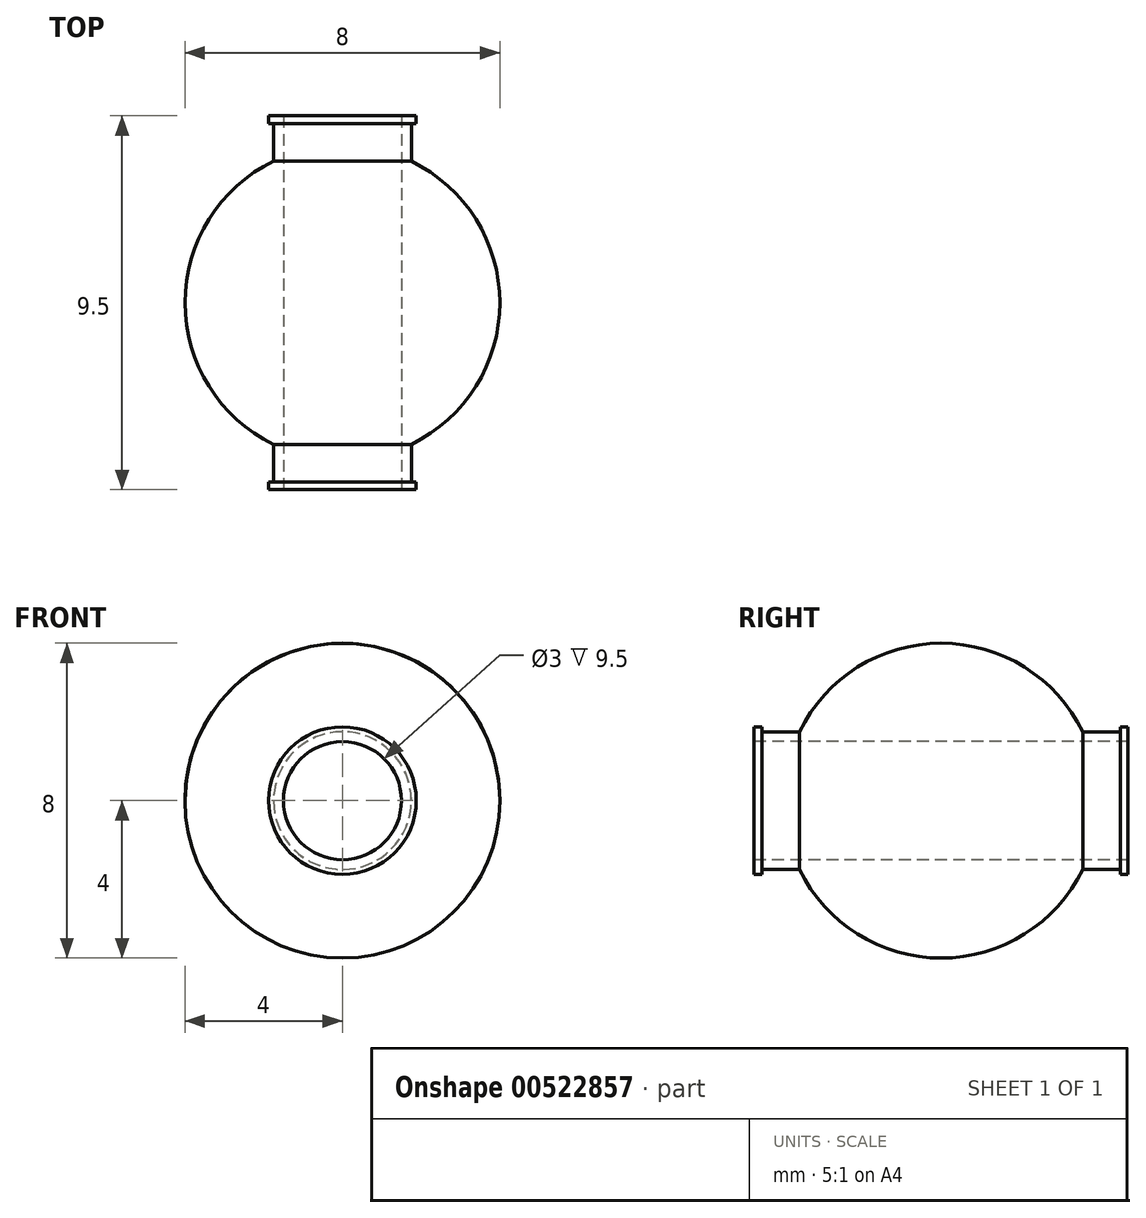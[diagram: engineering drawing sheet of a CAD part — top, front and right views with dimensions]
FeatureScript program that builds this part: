
annotation { "Feature Type Name" : "Feature", "Feature Type Description" : "" }
export const myFeature = defineFeature(function(context is Context, id is Id, definition is map)
    precondition{}
    {
        {
            var Q0;
            Q0=qCreatedBy(makeId("Front.planeOp"),FACE);
            var sketch = newSketch(context, id + "F0", { "sketchPlane" : qUnion([Q0])});
            skCircle(sketch, "E0", {"center": v(0, 0) * mm, "radius": 4 * mm});
            skLineSegment(sketch, "E1", {"start": v(-18.18, 0) * mm, "end": v(24.7, 0) * mm});
            skSolve(sketch);
        }
        {
            var Q0;
            {var subQ0=sQuery(id+"F0.wireOp",EDGE,"E1");var subQ1=sQuery(id+"F0.wireOp",EDGE,"E0");var subQ2=makeQuery(id+"F0.imprint","INTERSECT",VERTEX,{"disambiguationData":[OD(0.0)],"derivedFrom":[subQ1,subQ0]});Q0=makeQuery(id+"F0.imprint","IMPRINT",FACE,{"disambiguationData":[TD([[makeQuery(id+"F0.imprint","IMPRINT",EDGE,{"disambiguationData":[TD([[subQ2,1.0]])],"derivedFrom":subQ1}),1.0]])]});}
            var Q1;
            Q1=sQuery(id+"F0.wireOp",EDGE,"E1");
            revolve(context, id + "F1", {"surfaceOperationType" : NewSurfaceOperationType.NEW, "entities" : qUnion([Q0]), "axis" : qUnion([Q1]), "revolveType" : RevolveType.FULL});
        }
        {
            var Q0;
            Q0=qCreatedBy(makeId("Front.planeOp"),FACE);
            var sketch = newSketch(context, id + "F2", { "sketchPlane" : qUnion([Q0])});
            skCircle(sketch, "E2", {"center": v(0, 0) * mm, "radius": 1.5 * mm});
            skCircle(sketch, "E3", {"center": v(0, 0) * mm, "radius": 1.75 * mm});
            skSolve(sketch);
        }
        {
            var Q0;
            Q0=makeQuery(id+"F2.imprint","IMPRINT",FACE,{"disambiguationData":[TD([[makeQuery(id+"F2.imprint","IMPRINT",EDGE,{"derivedFrom":sQuery(id+"F2.wireOp",EDGE,"E2")}),1.0]])]});
            extrude(context, id + "F3", {"entities" : qUnion([Q0]), "operationType" : NewBodyOperationType.REMOVE, "endBound" : BoundingType.SYMMETRIC, "oppositeDirection" : true, "depth" : 25 * mm, "offsetDistance" : 25 * mm});
        }
        {
            var Q0;
            Q0=makeQuery(id+"F2.imprint","IMPRINT",FACE,{"disambiguationData":[TD([[makeQuery(id+"F2.imprint","IMPRINT",EDGE,{"derivedFrom":sQuery(id+"F2.wireOp",EDGE,"E2")}),-1.0]])]});
            extrude(context, id + "F4", {"entities" : qUnion([Q0]), "operationType" : NewBodyOperationType.ADD, "endBound" : BoundingType.SYMMETRIC, "depth" : 9.5 * mm, "offsetDistance" : 25 * mm});
        }
        {
            var Q0;
            Q0=makeQuery(id+"F4.opExtrude","CAP_FACE",FACE,{"disambiguationData":[OSD([sQuery(id+"F2.wireOp",EDGE,"E2"),sQuery(id+"F2.wireOp",EDGE,"E3")])],"isStart":false});
            var sketch = newSketch(context, id + "F5", { "sketchPlane" : qUnion([Q0])});
            skCircle(sketch, "E4", {"center": v(0, 0) * mm, "radius": 1.88 * mm});
            skSolve(sketch);
        }
        {
            var Q0;
            Q0=makeQuery(id+"F5.imprint","IMPRINT",FACE,{"disambiguationData":[TD([[makeQuery(id+"F5.imprint","IMPRINT",EDGE,{"derivedFrom":sQuery(id+"F5.wireOp",EDGE,"E4")}),1.0]])]});
            extrude(context, id + "F6", {"entities" : qUnion([Q0]), "operationType" : NewBodyOperationType.ADD, "oppositeDirection" : true, "depth" : .2 * mm, "offsetDistance" : 25 * mm});
        }
        {
            var Q0;
            Q0=makeQuery(id+"F4.opExtrude","CAP_FACE",FACE,{"disambiguationData":[OSD([sQuery(id+"F2.wireOp",EDGE,"E2"),sQuery(id+"F2.wireOp",EDGE,"E3")])],"isStart":true});
            var sketch = newSketch(context, id + "F7", { "sketchPlane" : qUnion([Q0])});
            skCircle(sketch, "E5", {"center": v(0, 0) * mm, "radius": 1.88 * mm});
            skSolve(sketch);
        }
        {
            var Q0;
            Q0=makeQuery(id+"F7.imprint","IMPRINT",FACE,{"disambiguationData":[TD([[makeQuery(id+"F7.imprint","IMPRINT",EDGE,{"derivedFrom":sQuery(id+"F7.wireOp",EDGE,"E5")}),1.0]])]});
            extrude(context, id + "F8", {"entities" : qUnion([Q0]), "operationType" : NewBodyOperationType.ADD, "oppositeDirection" : true, "depth" : .2 * mm, "offsetDistance" : 25 * mm});
        }
    });
